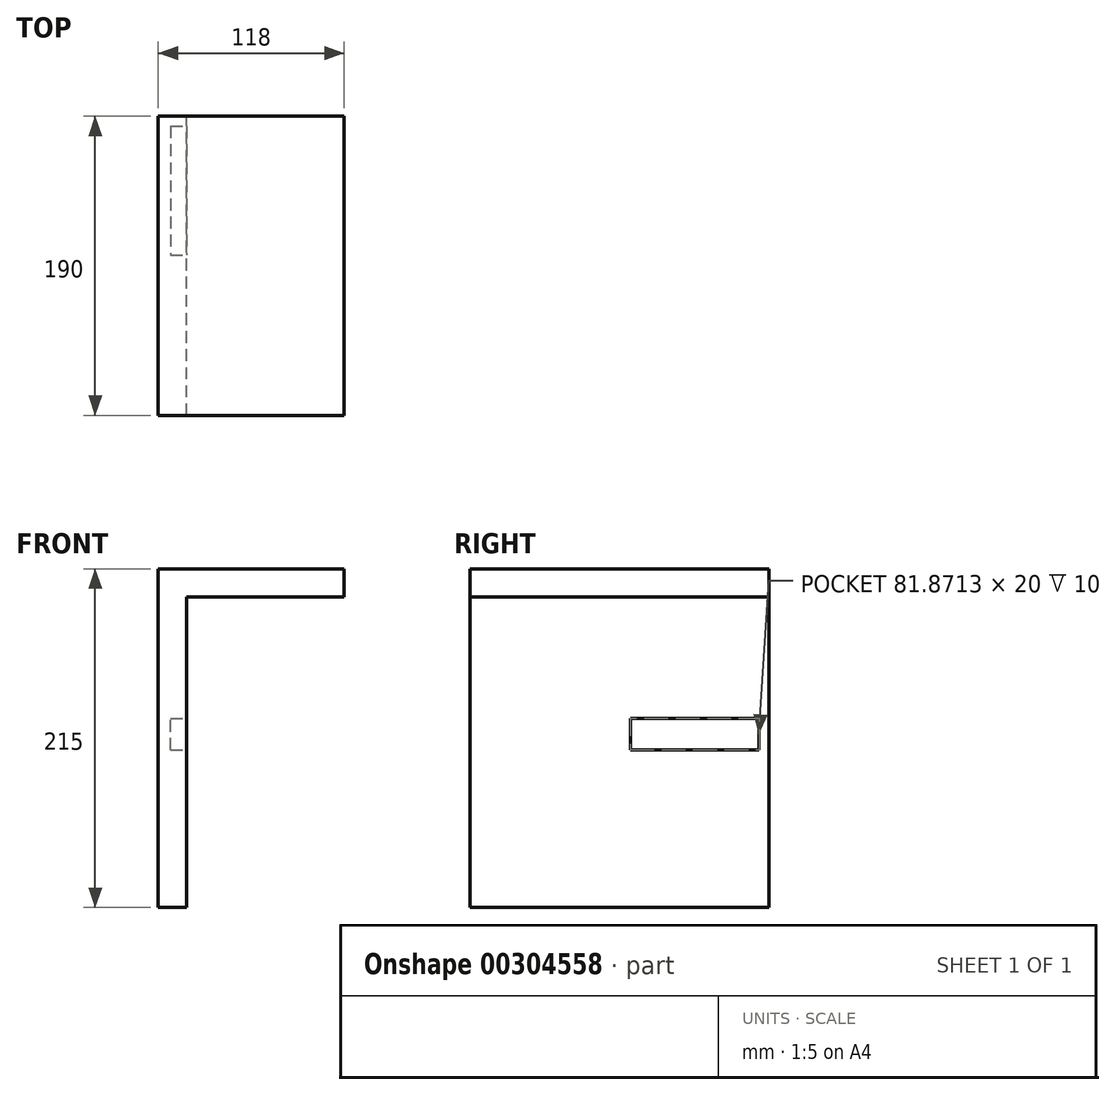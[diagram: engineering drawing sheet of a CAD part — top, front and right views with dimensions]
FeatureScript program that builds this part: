
annotation { "Feature Type Name" : "Feature", "Feature Type Description" : "" }
export const myFeature = defineFeature(function(context is Context, id is Id, definition is map)
    precondition{}
    {
        {
            var Q0;
            Q0=qCreatedBy(makeId("Front.planeOp"),FACE);
            var sketch = newSketch(context, id + "F0", { "sketchPlane" : qUnion([Q0])});
            skLineSegment(sketch, "E0", {"start": v(-8.67, 0) * mm, "end": v(9.33, 0) * mm});
            skLineSegment(sketch, "E1", {"start": v(-8.67, 0) * mm, "end": v(-8.67, 215) * mm});
            skLineSegment(sketch, "E2", {"start": v(-8.67, 215) * mm, "end": v(109.33, 215) * mm});
            skLineSegment(sketch, "E3", {"start": v(109.33, 215) * mm, "end": v(109.33, 197) * mm});
            skLineSegment(sketch, "E4", {"start": v(-8.67, 161.3) * mm, "end": v(9.33, 161.3) * mm, "construction": true});
            skLineSegment(sketch, "E5", {"start": v(9.33, 0) * mm, "end": v(9.33, 197) * mm});
            skLineSegment(sketch, "E6", {"start": v(9.33, 197) * mm, "end": v(109.33, 197) * mm});
            skSolve(sketch);
        }
        {
            var Q0;
            Q0=makeQuery(id+"F0.imprint","IMPRINT",FACE,{"disambiguationData":[TD([[makeQuery(id+"F0.imprint","IMPRINT",EDGE,{"derivedFrom":sQuery(id+"F0.wireOp",EDGE,"E0")}),1.0]])]});
            extrude(context, id + "F1", {"entities" : qUnion([Q0]), "depth" : 190 * mm});
        }
        {
            var Q0;
            Q0=makeQuery(id+"F1.opExtrude","SWEPT_FACE",FACE,{"disambiguationData":[OSD([sQuery(id+"F0.wireOp",EDGE,"E5")])]});
            var sketch = newSketch(context, id + "F2", { "sketchPlane" : qUnion([Q0])});
            skLineSegment(sketch, "E7", {"start": v(-47.26, 0) * mm, "end": v(-47.26, 100) * mm, "construction": true});
            skLineSegment(sketch, "E8", {"start": v(-95, 0) * mm, "end": v(-95, 197) * mm, "construction": true});
            skLineSegment(sketch, "E9.bottom", {"start": v(-6.33, 100) * mm, "end": v(-88.2, 100) * mm});
            skLineSegment(sketch, "E9.top", {"start": v(-6.33, 120) * mm, "end": v(-88.2, 120) * mm});
            skLineSegment(sketch, "E9.left", {"start": v(-6.33, 100) * mm, "end": v(-6.33, 120) * mm});
            skLineSegment(sketch, "E9.right", {"start": v(-88.2, 100) * mm, "end": v(-88.2, 120) * mm});
            skPoint(sketch, "E9.middle", {"position": v(-47.26, 110) * mm});
            skSolve(sketch);
        }
        {
            var Q0;
            Q0 = qSketchRegion(id + "F2", true);
            extrude(context, id + "F3", {"entities" : qUnion([Q0]), "operationType" : NewBodyOperationType.REMOVE, "oppositeDirection" : true, "depth" : 10 * mm});
        }
    });
